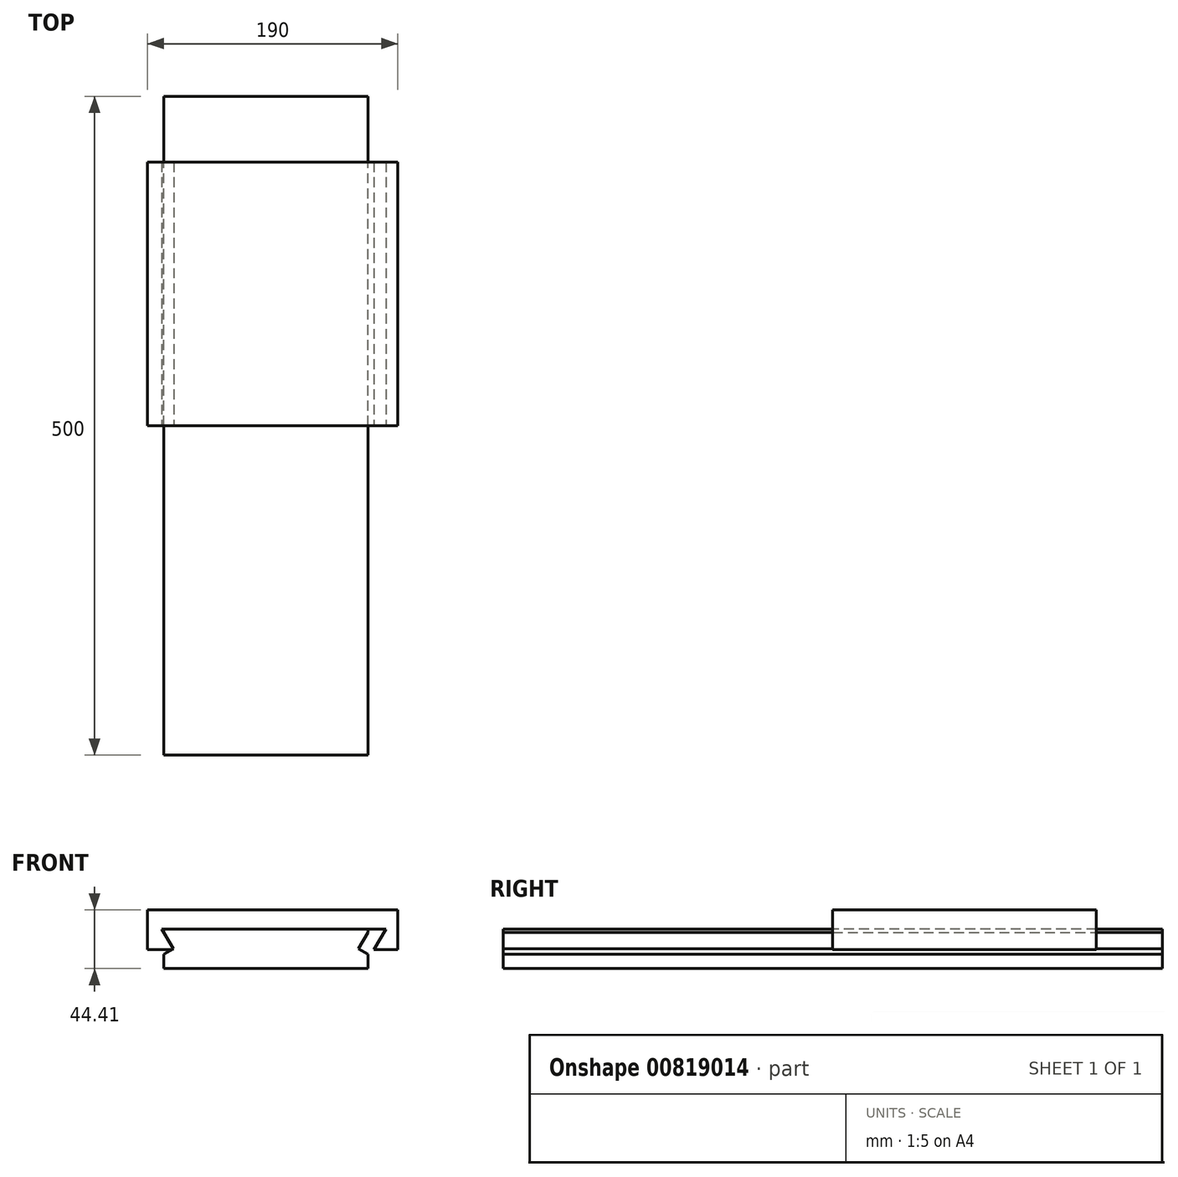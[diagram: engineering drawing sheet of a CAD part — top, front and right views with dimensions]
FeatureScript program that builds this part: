
annotation { "Feature Type Name" : "Feature", "Feature Type Description" : "" }
export const myFeature = defineFeature(function(context is Context, id is Id, definition is map)
    precondition{}
    {
        {
            var Q0;
            Q0=qCreatedBy(makeId("Front.planeOp"),FACE);
            var sketch = newSketch(context, id + "F0", { "sketchPlane" : qUnion([Q0])});
            skLineSegment(sketch, "E0.bottom", {"start": v(77.5, 15) * mm, "end": v(-77.5, 15) * mm});
            skLineSegment(sketch, "E0.top", {"start": v(77.5, -15) * mm, "end": v(-77.5, -15) * mm});
            skLineSegment(sketch, "E0.left", {"start": v(77.5, 15) * mm, "end": v(77.5, 12.5) * mm});
            skLineSegment(sketch, "E0.right", {"start": v(-77.5, 15) * mm, "end": v(-77.5, 12.5) * mm});
            skPoint(sketch, "E0.middle", {"position": v(0, 0) * mm});
            skLineSegment(sketch, "E1", {"start": v(-77.5, 12.5) * mm, "end": v(-70.28, 0) * mm});
            skPoint(sketch, "E1.endSnap0", {"position": v(-77.5, 0) * mm});
            skLineSegment(sketch, "E2", {"start": v(-70.28, 0) * mm, "end": v(-77.5, -4.17) * mm});
            skLineSegment(sketch, "E3", {"start": v(0, 15) * mm, "end": v(0, -15) * mm, "construction": true});
            skLineSegment(sketch, "E4.MirrorCS", {"start": v(77.5, 12.5) * mm, "end": v(70.28, 0) * mm});
            skLineSegment(sketch, "E5.MirrorCS", {"start": v(70.28, 0) * mm, "end": v(77.5, -4.17) * mm});
            skLineSegment(sketch, "E6.trimOffspring", {"start": v(-77.5, -4.17) * mm, "end": v(-77.5, -15) * mm});
            skLineSegment(sketch, "E7.trimOffspring", {"start": v(77.5, -4.17) * mm, "end": v(77.5, -15) * mm});
            skSolve(sketch);
        }
        {
            var Q0;
            Q0 = qSketchRegion(id + "F0", true);
            extrude(context, id + "F1", {"entities" : qUnion([Q0]), "endBound" : BoundingType.SYMMETRIC, "depth" : 500 * mm, "offsetDistance" : 25 * mm});
        }
        {
            var Q0;
            Q0=qCreatedBy(makeId("Front.planeOp"),FACE);
            var sketch = newSketch(context, id + "F2", { "sketchPlane" : qUnion([Q0])});
            skLineSegment(sketch, "E8", {"start": v(-90, -0.59) * mm, "end": v(-70, -0.59) * mm});
            skLineSegment(sketch, "E9", {"start": v(-70, -0.59) * mm, "end": v(-79, 15) * mm});
            skLineSegment(sketch, "E10", {"start": v(-79, 15) * mm, "end": v(91, 15) * mm});
            skLineSegment(sketch, "E11", {"start": v(91, 15) * mm, "end": v(82, -0.59) * mm});
            skLineSegment(sketch, "E12", {"start": v(82, -0.59) * mm, "end": v(100, -0.59) * mm});
            skLineSegment(sketch, "E13", {"start": v(100, -0.59) * mm, "end": v(100, 29.41) * mm});
            skLineSegment(sketch, "E14", {"start": v(100, 29.41) * mm, "end": v(-90, 29.41) * mm});
            skLineSegment(sketch, "E15", {"start": v(-90, 29.41) * mm, "end": v(-90, -0.59) * mm});
            skLineSegment(sketch, "E16", {"start": v(0, 46.7) * mm, "end": v(0, 15) * mm, "construction": true});
            skSolve(sketch);
        }
        {
            var Q0;
            Q0=makeQuery(id+"F2.imprint","IMPRINT",FACE,{"disambiguationData":[TD([[makeQuery(id+"F2.imprint","IMPRINT",EDGE,{"derivedFrom":sQuery(id+"F2.wireOp",EDGE,"E8")}),1.0]])]});
            extrude(context, id + "F3", {"entities" : qUnion([Q0]), "oppositeDirection" : true, "depth" : 200 * mm, "offsetDistance" : 25 * mm});
        }
    });
